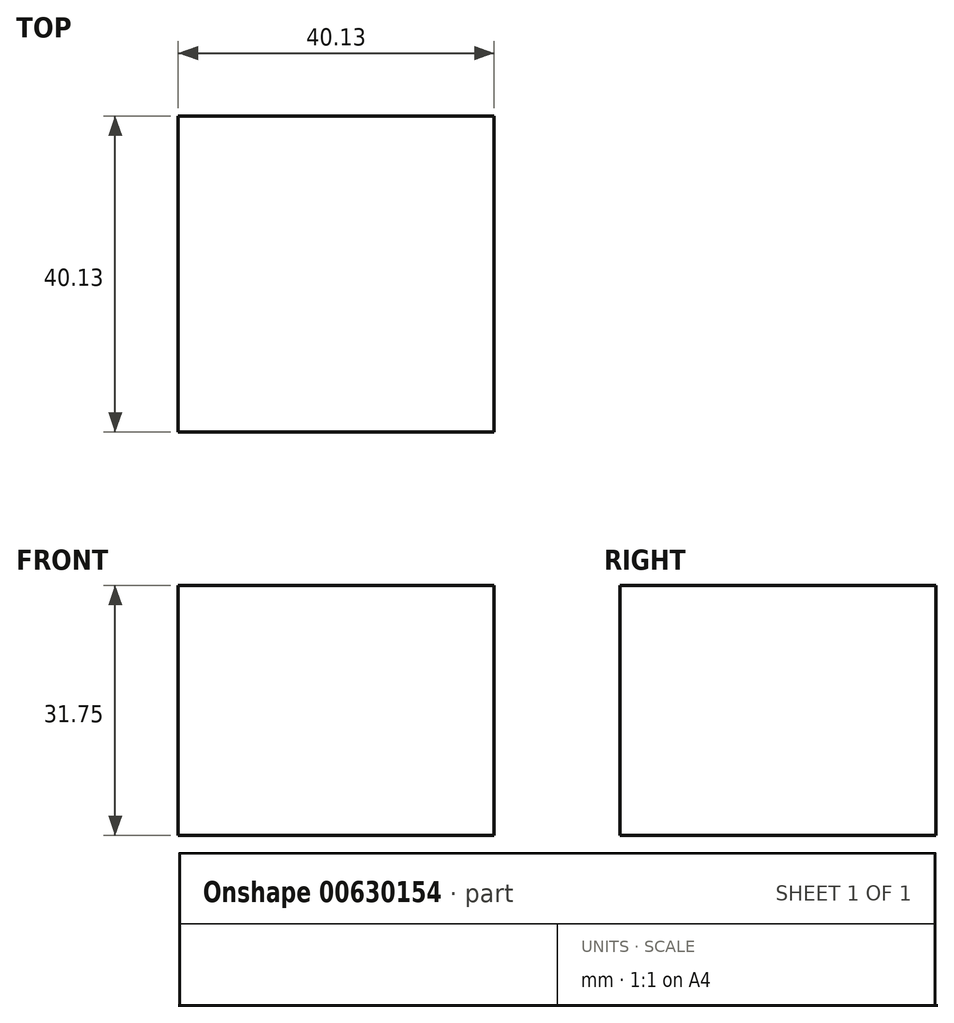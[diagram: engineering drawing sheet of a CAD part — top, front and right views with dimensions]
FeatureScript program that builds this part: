
annotation { "Feature Type Name" : "Feature", "Feature Type Description" : "" }
export const myFeature = defineFeature(function(context is Context, id is Id, definition is map)
    precondition{}
    {
        {
            var Q0;
            Q0=qCreatedBy(makeId("Top.planeOp"),FACE);
            var sketch = newSketch(context, id + "F0", { "sketchPlane" : qUnion([Q0])});
            skLineSegment(sketch, "E0.bottom", {"start": v(0, 0) * mm, "end": v(40.13, 0) * mm});
            skLineSegment(sketch, "E0.top", {"start": v(0, 40.13) * mm, "end": v(40.13, 40.13) * mm});
            skLineSegment(sketch, "E0.left", {"start": v(0, 0) * mm, "end": v(0, 40.13) * mm});
            skLineSegment(sketch, "E0.right", {"start": v(40.13, 0) * mm, "end": v(40.13, 40.13) * mm});
            skSolve(sketch);
        }
        {
            var Q0;
            Q0=makeQuery(id+"F0.imprint","IMPRINT",FACE,{"disambiguationData":[TD([[makeQuery(id+"F0.imprint","IMPRINT",EDGE,{"derivedFrom":sQuery(id+"F0.wireOp",EDGE,"E0.bottom")}),1.0]])]});
            extrude(context, id + "F1", {"entities" : qUnion([Q0]), "depth" : 31.75 * mm, "offsetDistance" : 25.4 * mm});
        }
    });
